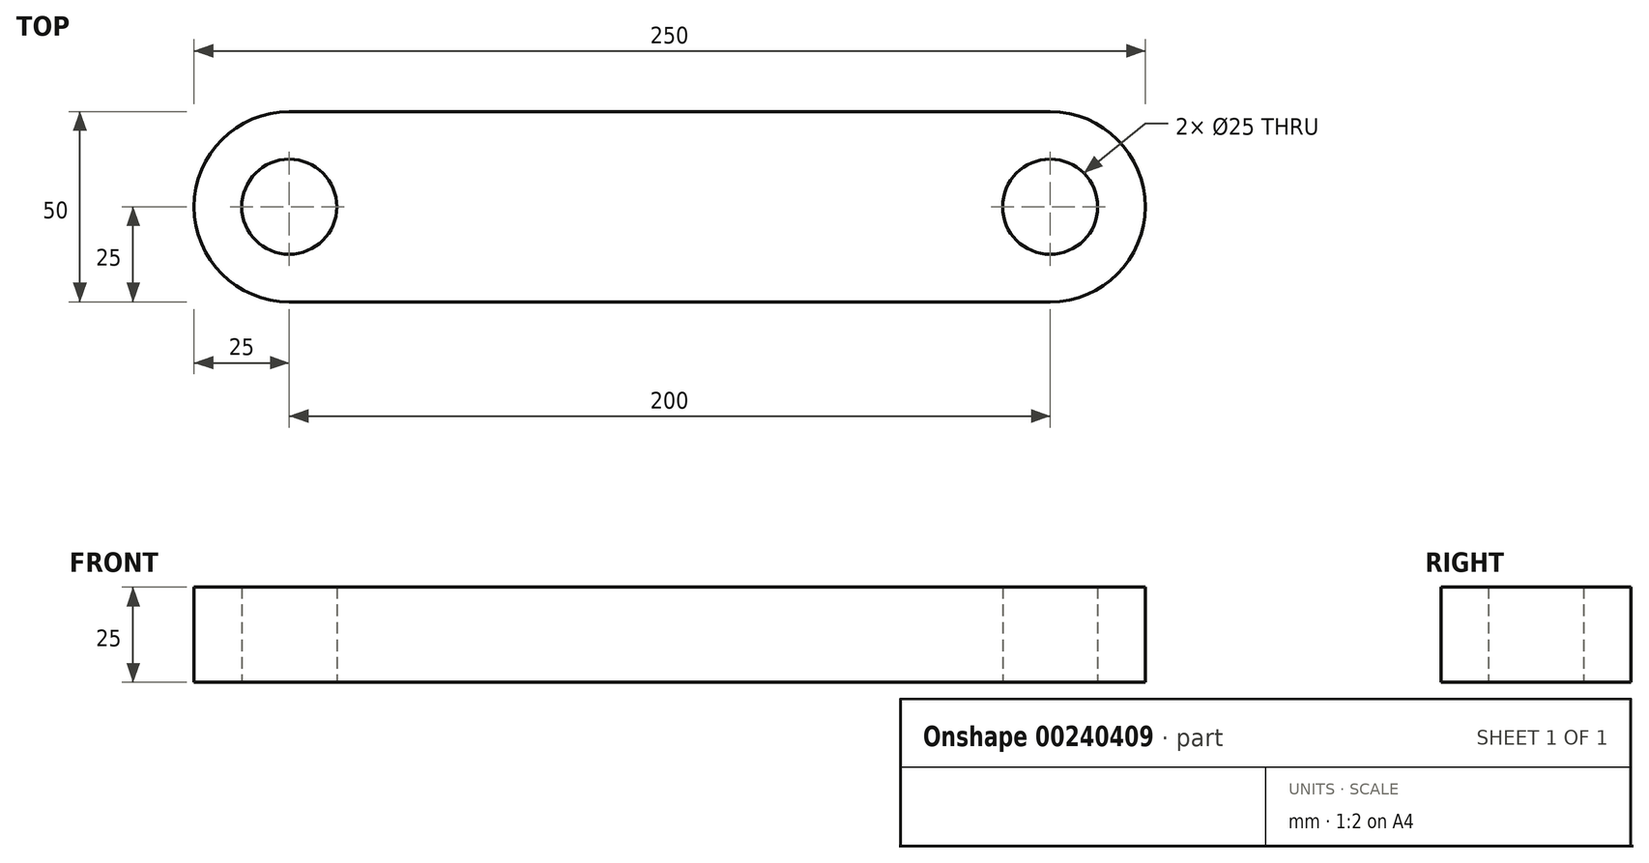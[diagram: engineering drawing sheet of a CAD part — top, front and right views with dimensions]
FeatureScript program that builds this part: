
annotation { "Feature Type Name" : "Feature", "Feature Type Description" : "" }
export const myFeature = defineFeature(function(context is Context, id is Id, definition is map)
    precondition{}
    {
        {
            var Q0;
            Q0=qCreatedBy(makeId("Top.planeOp"),FACE);
            var sketch = newSketch(context, id + "F0", { "sketchPlane" : qUnion([Q0])});
            skLineSegment(sketch, "E0.rect.bottom", {"start": v(100, 25) * mm, "end": v(-100, 25) * mm});
            skLineSegment(sketch, "E0.rect.top", {"start": v(100, -25) * mm, "end": v(-100, -25) * mm});
            skPoint(sketch, "E0.rect.middle", {"position": v(0, 0) * mm});
            skArc(sketch, "E1", {"start": v(-100, 25) * mm, "mid": v(-125, 0) * mm, "end": v(-100, -25) * mm});
            skArc(sketch, "E2", {"start": v(100, -25) * mm, "mid": v(125, 0) * mm, "end": v(100, 25) * mm});
            skCircle(sketch, "E3", {"center": v(100, 0) * mm, "radius": 12.5 * mm});
            skCircle(sketch, "E4", {"center": v(-100, 0) * mm, "radius": 12.5 * mm});
            skSolve(sketch);
        }
        {
            var Q0;
            Q0=qSketchRegion(id+"F0",true);
            extrude(context, id + "F1", {"entities" : qUnion([Q0]), "depth" : 25 * mm});
        }
    });
